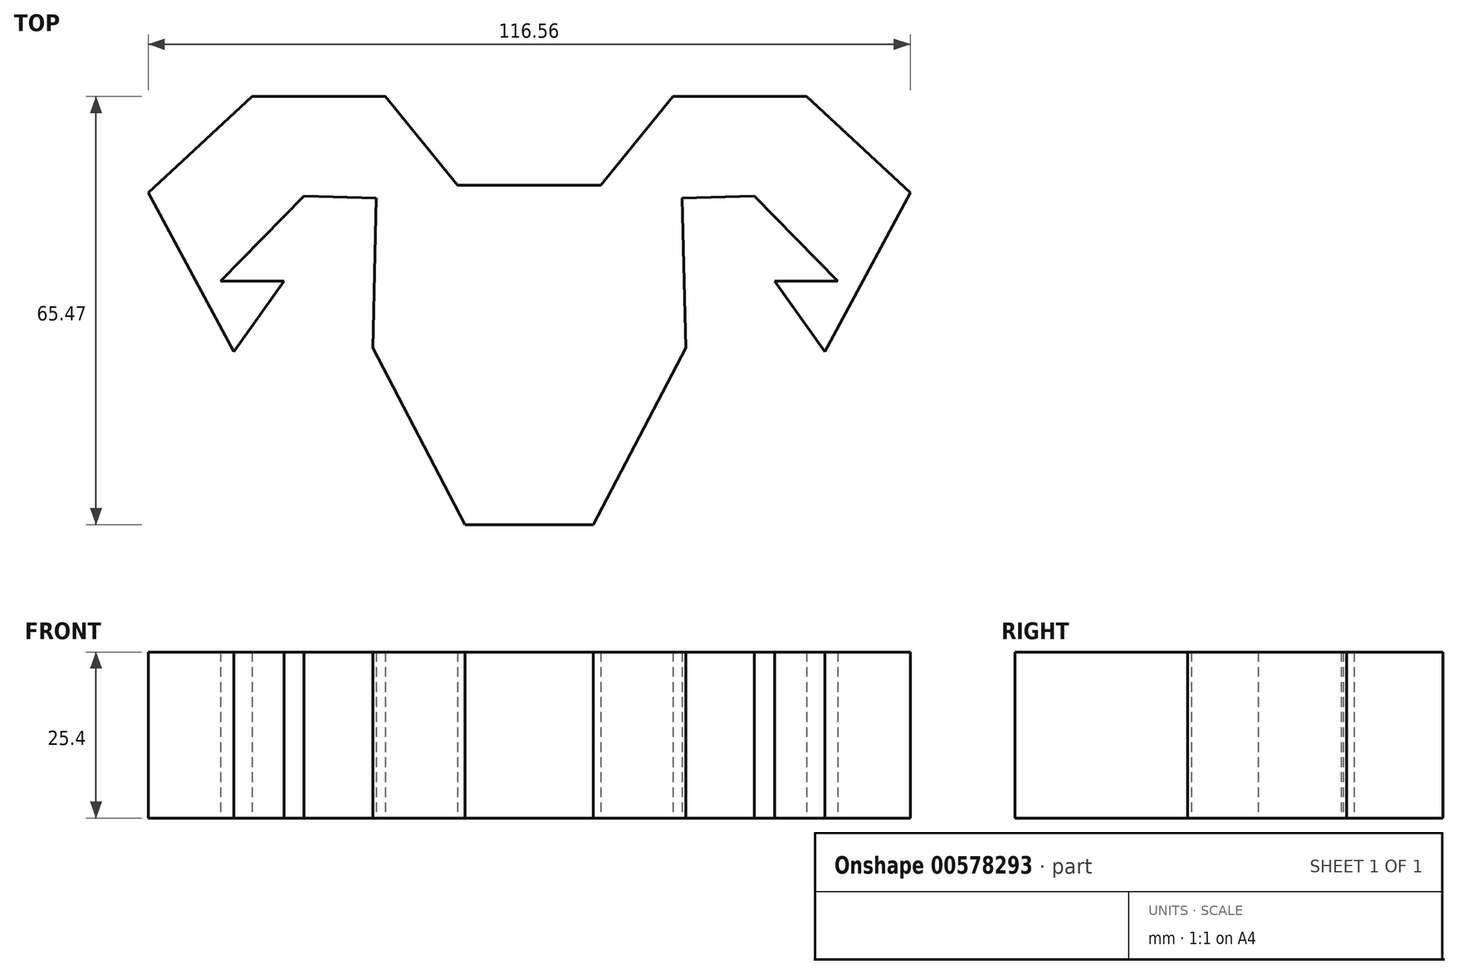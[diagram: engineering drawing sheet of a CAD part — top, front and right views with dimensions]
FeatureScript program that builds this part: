
annotation { "Feature Type Name" : "Feature", "Feature Type Description" : "" }
export const myFeature = defineFeature(function(context is Context, id is Id, definition is map)
    precondition{}
    {
        {
            var Q0;
            Q0=qCreatedBy(makeId("Top.planeOp"),FACE);
            var sketch = newSketch(context, id + "F0", { "sketchPlane" : qUnion([Q0])});
            skLineSegment(sketch, "E0", {"start": v(-23.4, 49.97) * mm, "end": v(-23.95, 26.99) * mm});
            skLineSegment(sketch, "E1", {"start": v(-23.95, 26.99) * mm, "end": v(-9.83, 0) * mm});
            skLineSegment(sketch, "E2", {"start": v(-9.83, 0) * mm, "end": v(0, 0) * mm});
            skLineSegment(sketch, "E3", {"start": v(-23.4, 49.97) * mm, "end": v(-34.46, 50.23) * mm});
            skLineSegment(sketch, "E4", {"start": v(-42.4, 65.47) * mm, "end": v(-22, 65.47) * mm});
            skLineSegment(sketch, "E5", {"start": v(-22, 65.47) * mm, "end": v(-10.94, 51.9) * mm});
            skLineSegment(sketch, "E6", {"start": v(-10.94, 51.9) * mm, "end": v(0, 51.9) * mm});
            skLineSegment(sketch, "E7", {"start": v(-42.4, 65.47) * mm, "end": v(-58.28, 50.8) * mm});
            skLineSegment(sketch, "E8", {"start": v(-37.51, 37.23) * mm, "end": v(-47.2, 37.23) * mm});
            skLineSegment(sketch, "E9", {"start": v(-34.46, 50.23) * mm, "end": v(-47.2, 37.23) * mm});
            skLineSegment(sketch, "E10", {"start": v(0, 51.9) * mm, "end": v(0, 0) * mm});
            skLineSegment(sketch, "E11.MirrorCS", {"start": v(10.94, 51.9) * mm, "end": v(0, 51.9) * mm});
            skLineSegment(sketch, "E12.MirrorCS", {"start": v(22, 65.47) * mm, "end": v(10.94, 51.9) * mm});
            skLineSegment(sketch, "E13.MirrorCS", {"start": v(42.4, 65.47) * mm, "end": v(22, 65.47) * mm});
            skLineSegment(sketch, "E14.MirrorCS", {"start": v(23.4, 49.97) * mm, "end": v(23.95, 26.99) * mm});
            skLineSegment(sketch, "E15.MirrorCS", {"start": v(23.95, 26.99) * mm, "end": v(9.83, 0) * mm});
            skLineSegment(sketch, "E16.MirrorCS", {"start": v(9.83, 0) * mm, "end": v(0, 0) * mm});
            skLineSegment(sketch, "E17.MirrorCS", {"start": v(23.4, 49.97) * mm, "end": v(34.46, 50.23) * mm});
            skLineSegment(sketch, "E18", {"start": v(-58.28, 50.8) * mm, "end": v(-45.22, 26.46) * mm});
            skLineSegment(sketch, "E19", {"start": v(-45.22, 26.46) * mm, "end": v(-37.51, 37.23) * mm});
            skLineSegment(sketch, "E20.MirrorCS", {"start": v(42.4, 65.47) * mm, "end": v(58.28, 50.8) * mm});
            skLineSegment(sketch, "E21.MirrorCS", {"start": v(58.28, 50.8) * mm, "end": v(45.22, 26.46) * mm});
            skLineSegment(sketch, "E22.MirrorCS", {"start": v(34.46, 50.23) * mm, "end": v(47.2, 37.23) * mm});
            skLineSegment(sketch, "E23.MirrorCS", {"start": v(45.22, 26.46) * mm, "end": v(37.51, 37.23) * mm});
            skLineSegment(sketch, "E24.MirrorCS", {"start": v(37.51, 37.23) * mm, "end": v(47.2, 37.23) * mm});
            skSolve(sketch);
        }
        {
            var Q0;
            Q0 = qSketchRegion(id + "F0", true);
            extrude(context, id + "F1", {"entities" : qUnion([Q0]), "depth" : 25.4 * mm, "offsetDistance" : 25.4 * mm});
        }
    });
